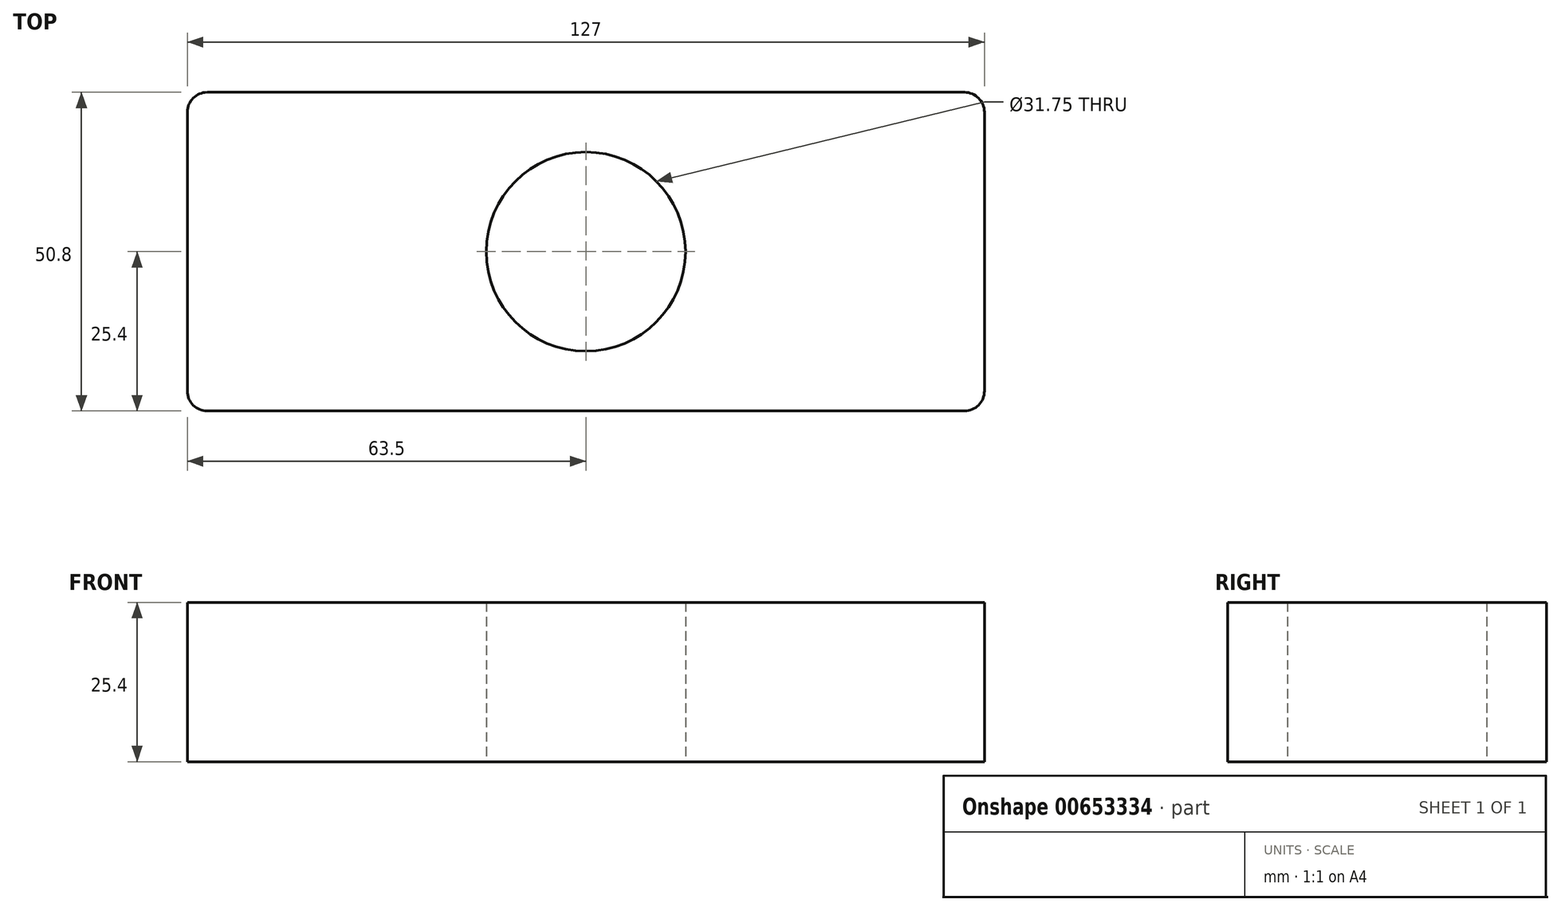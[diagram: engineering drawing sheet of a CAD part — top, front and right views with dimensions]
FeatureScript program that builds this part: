
annotation { "Feature Type Name" : "Feature", "Feature Type Description" : "" }
export const myFeature = defineFeature(function(context is Context, id is Id, definition is map)
    precondition{}
    {
        {
            var Q0;
            Q0=qCreatedBy(makeId("Top.planeOp"),FACE);
            var sketch = newSketch(context, id + "F0", { "sketchPlane" : qUnion([Q0])});
            skLineSegment(sketch, "E0.bottom", {"start": v(-60.32, -25.4) * mm, "end": v(60.33, -25.4) * mm});
            skLineSegment(sketch, "E0.top", {"start": v(-60.33, 25.4) * mm, "end": v(60.32, 25.4) * mm});
            skLineSegment(sketch, "E0.left", {"start": v(-63.5, -22.23) * mm, "end": v(-63.5, 22.23) * mm});
            skLineSegment(sketch, "E0.right", {"start": v(63.5, -22.22) * mm, "end": v(63.5, 22.23) * mm});
            skPoint(sketch, "E0.middle", {"position": v(0, 0) * mm});
            skCircle(sketch, "E1", {"center": v(0, 0) * mm, "radius": 15.88 * mm});
            skPoint(sketch, "E2.visualSharp", {"position": v(-63.5, 25.4) * mm});
            skArc(sketch, "E2.filletArc", {"start": v(-60.33, 25.4) * mm, "mid": v(-62.57, 24.47) * mm, "end": v(-63.5, 22.23) * mm});
            skPoint(sketch, "E3.visualSharp", {"position": v(-63.5, -25.4) * mm});
            skArc(sketch, "E3.filletArc", {"start": v(-63.5, -22.23) * mm, "mid": v(-62.57, -24.47) * mm, "end": v(-60.32, -25.4) * mm});
            skPoint(sketch, "E4.visualSharp", {"position": v(63.5, 25.4) * mm});
            skArc(sketch, "E4.filletArc", {"start": v(63.5, 22.23) * mm, "mid": v(62.57, 24.47) * mm, "end": v(60.32, 25.4) * mm});
            skPoint(sketch, "E5.visualSharp", {"position": v(63.5, -25.4) * mm});
            skArc(sketch, "E5.filletArc", {"start": v(60.33, -25.4) * mm, "mid": v(62.57, -24.47) * mm, "end": v(63.5, -22.22) * mm});
            skSolve(sketch);
        }
        {
            var Q0;
            Q0 = qSketchRegion(id + "F0", true);
            extrude(context, id + "F1", {"entities" : qUnion([Q0]), "depth" : 25.4 * mm, "offsetDistance" : 25.4 * mm});
        }
    });
